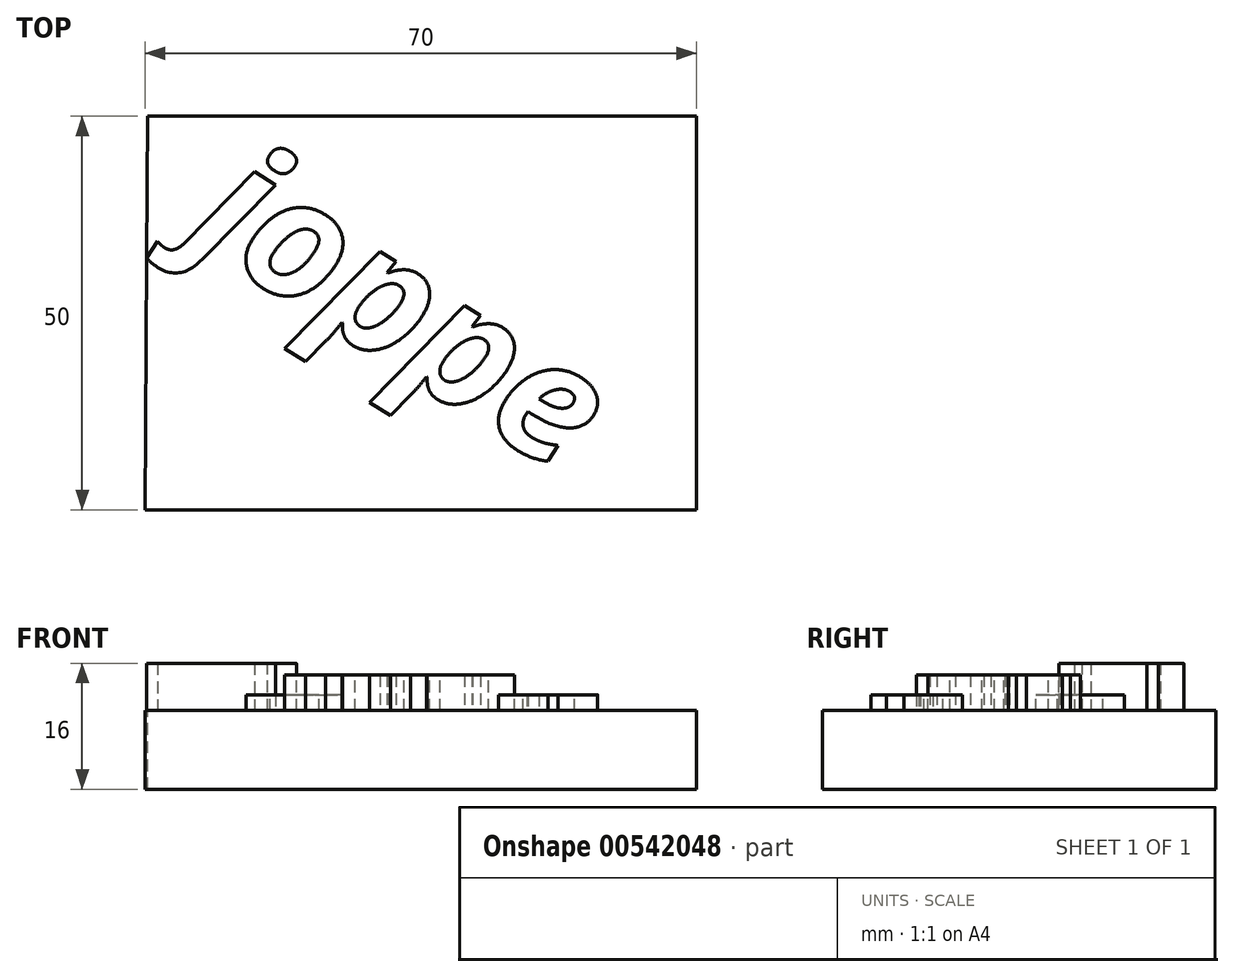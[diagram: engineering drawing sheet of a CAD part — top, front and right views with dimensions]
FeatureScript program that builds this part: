
annotation { "Feature Type Name" : "Feature", "Feature Type Description" : "" }
export const myFeature = defineFeature(function(context is Context, id is Id, definition is map)
    precondition{}
    {
        {
            var Q0;
            Q0=qCreatedBy(makeId("Top.planeOp"),FACE);
            var sketch = newSketch(context, id + "F0", { "sketchPlane" : qUnion([Q0])});
            skLineSegment(sketch, "E0", {"start": v(-35.08, -30) * mm, "end": v(34.92, -30) * mm});
            skLineSegment(sketch, "E1", {"start": v(34.92, -30) * mm, "end": v(34.92, 20) * mm});
            skLineSegment(sketch, "E2", {"start": v(34.92, 20) * mm, "end": v(-34.8, 20) * mm});
            skLineSegment(sketch, "E3", {"start": v(-34.8, 20) * mm, "end": v(-35.08, -30) * mm});
            skSolve(sketch);
        }
        {
            var Q0;
            Q0=makeQuery(id+"F0.imprint","IMPRINT",FACE,{"disambiguationData":[TD([[makeQuery(id+"F0.imprint","IMPRINT",EDGE,{"derivedFrom":sQuery(id+"F0.wireOp",EDGE,"E0")}),1.0]])]});
            extrude(context, id + "F1", {"entities" : qUnion([Q0]), "oppositeDirection" : true, "depth" : 10 * mm, "offsetDistance" : 25 * mm});
        }
        {
            var Q0;
            Q0=qCreatedBy(makeId("Top.planeOp"),FACE);
            var sketch = newSketch(context, id + "F2", { "sketchPlane" : qUnion([Q0])});
            skText(sketch, "E4", { "text": "joppe", "fontName": "OpenSans-BoldItalic.ttf"});
            const initialGuessF2  = {"E4": [-0.02994, 0.00464, 0.84355, -0.53705, 0.01544]};
            skSetInitialGuess(sketch, initialGuessF2);
            skSolve(sketch);
        }
        {
            var Q0;
            Q0 = qSketchRegion(id + "F2", true);
            extrude(context, id + "F3", {"entities" : qUnion([Q0]), "operationType" : NewBodyOperationType.ADD, "depth" : 2 * mm, "offsetDistance" : 25 * mm});
        }
        {
            var Q0;
            Q0=makeQuery(id+"F3.opExtrude","CAP_FACE",FACE,{"disambiguationData":[OSD([sQuery(id+"F2.wireOp",EDGE,"E4.sketch_text.stroke-0"),sQuery(id+"F2.wireOp",EDGE,"E4.sketch_text.stroke-1"),sQuery(id+"F2.wireOp",EDGE,"E4.sketch_text.stroke-2"),sQuery(id+"F2.wireOp",EDGE,"E4.sketch_text.stroke-3"),sQuery(id+"F2.wireOp",EDGE,"E4.sketch_text.stroke-4"),sQuery(id+"F2.wireOp",EDGE,"E4.sketch_text.stroke-5"),sQuery(id+"F2.wireOp",EDGE,"E4.sketch_text.stroke-6"),sQuery(id+"F2.wireOp",EDGE,"E4.sketch_text.stroke-7")])],"isStart":false});
            var Q1;
            Q1=makeQuery(id+"F3.opExtrude","CAP_FACE",FACE,{"disambiguationData":[OSD([sQuery(id+"F2.wireOp",EDGE,"E4.sketch_text.stroke-8"),sQuery(id+"F2.wireOp",EDGE,"E4.sketch_text.stroke-9"),sQuery(id+"F2.wireOp",EDGE,"E4.sketch_text.stroke-10"),sQuery(id+"F2.wireOp",EDGE,"E4.sketch_text.stroke-11"),sQuery(id+"F2.wireOp",EDGE,"E4.sketch_text.stroke-12"),sQuery(id+"F2.wireOp",EDGE,"E4.sketch_text.stroke-13"),sQuery(id+"F2.wireOp",EDGE,"E4.sketch_text.stroke-14")])],"isStart":false});
            extrude(context, id + "F4", {"entities" : qUnion([Q0, Q1]), "operationType" : NewBodyOperationType.ADD, "depth" : 4 * mm, "offsetDistance" : 25 * mm});
        }
        {
            var Q0;
            Q0=makeQuery(id+"F3.opExtrude","CAP_FACE",FACE,{"disambiguationData":[OSD([sQuery(id+"F2.wireOp",EDGE,"E4.sketch_text.stroke-33"),sQuery(id+"F2.wireOp",EDGE,"E4.sketch_text.stroke-34"),sQuery(id+"F2.wireOp",EDGE,"E4.sketch_text.stroke-35"),sQuery(id+"F2.wireOp",EDGE,"E4.sketch_text.stroke-36"),sQuery(id+"F2.wireOp",EDGE,"E4.sketch_text.stroke-37"),sQuery(id+"F2.wireOp",EDGE,"E4.sketch_text.stroke-38"),sQuery(id+"F2.wireOp",EDGE,"E4.sketch_text.stroke-39"),sQuery(id+"F2.wireOp",EDGE,"E4.sketch_text.stroke-40"),sQuery(id+"F2.wireOp",EDGE,"E4.sketch_text.stroke-41"),sQuery(id+"F2.wireOp",EDGE,"E4.sketch_text.stroke-42"),sQuery(id+"F2.wireOp",EDGE,"E4.sketch_text.stroke-43"),sQuery(id+"F2.wireOp",EDGE,"E4.sketch_text.stroke-44"),sQuery(id+"F2.wireOp",EDGE,"E4.sketch_text.stroke-45"),sQuery(id+"F2.wireOp",EDGE,"E4.sketch_text.stroke-46"),sQuery(id+"F2.wireOp",EDGE,"E4.sketch_text.stroke-47"),sQuery(id+"F2.wireOp",EDGE,"E4.sketch_text.stroke-48"),sQuery(id+"F2.wireOp",EDGE,"E4.sketch_text.stroke-49"),sQuery(id+"F2.wireOp",EDGE,"E4.sketch_text.stroke-50"),sQuery(id+"F2.wireOp",EDGE,"E4.sketch_text.stroke-51"),sQuery(id+"F2.wireOp",EDGE,"E4.sketch_text.stroke-52"),sQuery(id+"F2.wireOp",EDGE,"E4.sketch_text.stroke-53"),sQuery(id+"F2.wireOp",EDGE,"E4.sketch_text.stroke-54"),sQuery(id+"F2.wireOp",EDGE,"E4.sketch_text.stroke-55"),sQuery(id+"F2.wireOp",EDGE,"E4.sketch_text.stroke-56"),sQuery(id+"F2.wireOp",EDGE,"E4.sketch_text.stroke-57")])],"isStart":false});
            var Q1;
            Q1=makeQuery(id+"F3.opExtrude","CAP_FACE",FACE,{"disambiguationData":[OSD([sQuery(id+"F2.wireOp",EDGE,"E4.sketch_text.stroke-58"),sQuery(id+"F2.wireOp",EDGE,"E4.sketch_text.stroke-59"),sQuery(id+"F2.wireOp",EDGE,"E4.sketch_text.stroke-60"),sQuery(id+"F2.wireOp",EDGE,"E4.sketch_text.stroke-61"),sQuery(id+"F2.wireOp",EDGE,"E4.sketch_text.stroke-62"),sQuery(id+"F2.wireOp",EDGE,"E4.sketch_text.stroke-63"),sQuery(id+"F2.wireOp",EDGE,"E4.sketch_text.stroke-64"),sQuery(id+"F2.wireOp",EDGE,"E4.sketch_text.stroke-65"),sQuery(id+"F2.wireOp",EDGE,"E4.sketch_text.stroke-66"),sQuery(id+"F2.wireOp",EDGE,"E4.sketch_text.stroke-67"),sQuery(id+"F2.wireOp",EDGE,"E4.sketch_text.stroke-68"),sQuery(id+"F2.wireOp",EDGE,"E4.sketch_text.stroke-69"),sQuery(id+"F2.wireOp",EDGE,"E4.sketch_text.stroke-70"),sQuery(id+"F2.wireOp",EDGE,"E4.sketch_text.stroke-71"),sQuery(id+"F2.wireOp",EDGE,"E4.sketch_text.stroke-72"),sQuery(id+"F2.wireOp",EDGE,"E4.sketch_text.stroke-73"),sQuery(id+"F2.wireOp",EDGE,"E4.sketch_text.stroke-74"),sQuery(id+"F2.wireOp",EDGE,"E4.sketch_text.stroke-75"),sQuery(id+"F2.wireOp",EDGE,"E4.sketch_text.stroke-76"),sQuery(id+"F2.wireOp",EDGE,"E4.sketch_text.stroke-77"),sQuery(id+"F2.wireOp",EDGE,"E4.sketch_text.stroke-78"),sQuery(id+"F2.wireOp",EDGE,"E4.sketch_text.stroke-79"),sQuery(id+"F2.wireOp",EDGE,"E4.sketch_text.stroke-80"),sQuery(id+"F2.wireOp",EDGE,"E4.sketch_text.stroke-81"),sQuery(id+"F2.wireOp",EDGE,"E4.sketch_text.stroke-82")])],"isStart":false});
            extrude(context, id + "F5", {"entities" : qUnion([Q0, Q1]), "operationType" : NewBodyOperationType.ADD, "depth" : 2.5 * mm, "offsetDistance" : 25 * mm});
        }
    });
